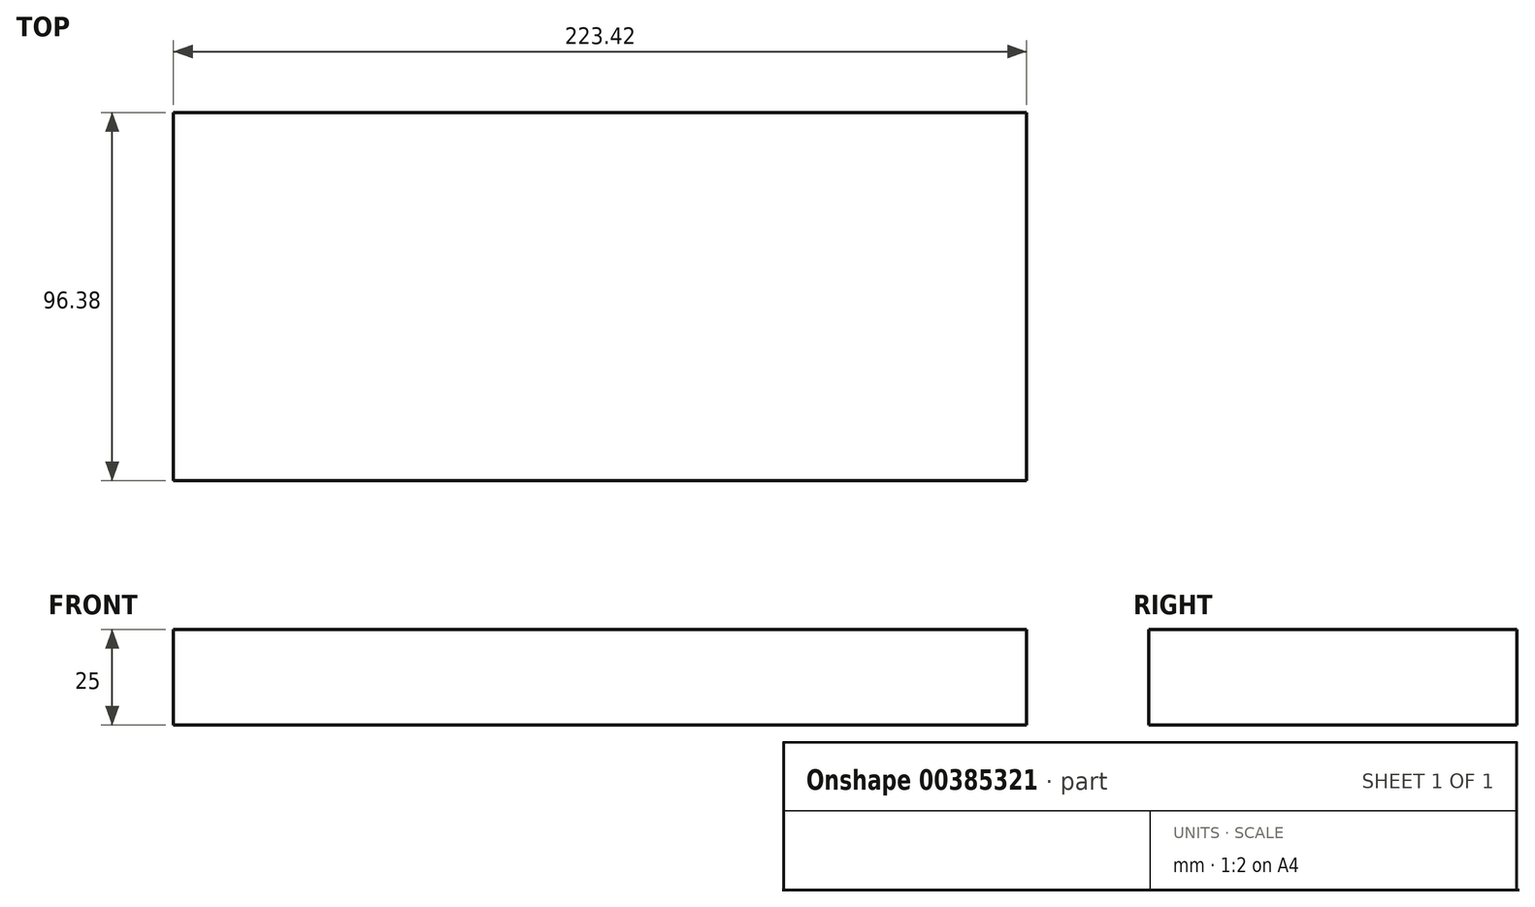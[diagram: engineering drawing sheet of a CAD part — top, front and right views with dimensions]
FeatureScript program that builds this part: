
annotation { "Feature Type Name" : "Feature", "Feature Type Description" : "" }
export const myFeature = defineFeature(function(context is Context, id is Id, definition is map)
    precondition{}
    {
        {
            var Q0;
            Q0=qCreatedBy(makeId("Top.planeOp"),FACE);
            var sketch = newSketch(context, id + "F0", { "sketchPlane" : qUnion([Q0])});
            skLineSegment(sketch, "E0.bottom", {"start": v(111.7, -48.2) * mm, "end": v(-111.7, -48.2) * mm});
            skLineSegment(sketch, "E0.top", {"start": v(111.7, 48.2) * mm, "end": v(-111.7, 48.2) * mm});
            skLineSegment(sketch, "E0.left", {"start": v(111.7, -48.2) * mm, "end": v(111.7, 48.2) * mm});
            skLineSegment(sketch, "E0.right", {"start": v(-111.7, -48.2) * mm, "end": v(-111.7, 48.2) * mm});
            skPoint(sketch, "E0.middle", {"position": v(0, 0) * mm});
            skSolve(sketch);
        }
        {
            var Q0;
            Q0 = qSketchRegion(id + "F0", true);
            extrude(context, id + "F1", {"entities" : qUnion([Q0]), "depth" : 25 * mm});
        }
        {
            var Q0;
            Q0=qCreatedBy(makeId("Front.planeOp"),FACE);
            var sketch = newSketch(context, id + "F2", { "sketchPlane" : qUnion([Q0])});
            skFitSpline(sketch, "E1", {"points": [v(-91.7, 91.83) * mm, v(31.44, 137.42) * mm, v(53.76, 112.62) * mm, v(88.73, 102.25) * mm], "startDerivative": vector(309.44, 164.43) * mm, "endDerivative": vector(153.87, -15.36) * mm});
            skLineSegment(sketch, "E2", {"start": v(88.73, 102.25) * mm, "end": v(145.72, 96.56) * mm});
            skLineSegment(sketch, "E3", {"start": v(-112.16, 148.8) * mm, "end": v(-25.48, 182) * mm});
            skSolve(sketch);
        }
        {
            var Q0;
            Q0=sQuery(id+"F2.wireOp",VERTEX,"E1.0.internal");
            var Q1;
            Q1=sQuery(id+"F2.wireOp",EDGE,"E1");
            cPlane(context, id + "F3", {"entities" : qUnion([Q0, Q1]), "cplaneType" : CPlaneType.CURVE_POINT, "offset" : 25 * mm, "width" : 150 * mm, "height" : 150 * mm});
        }
    });
